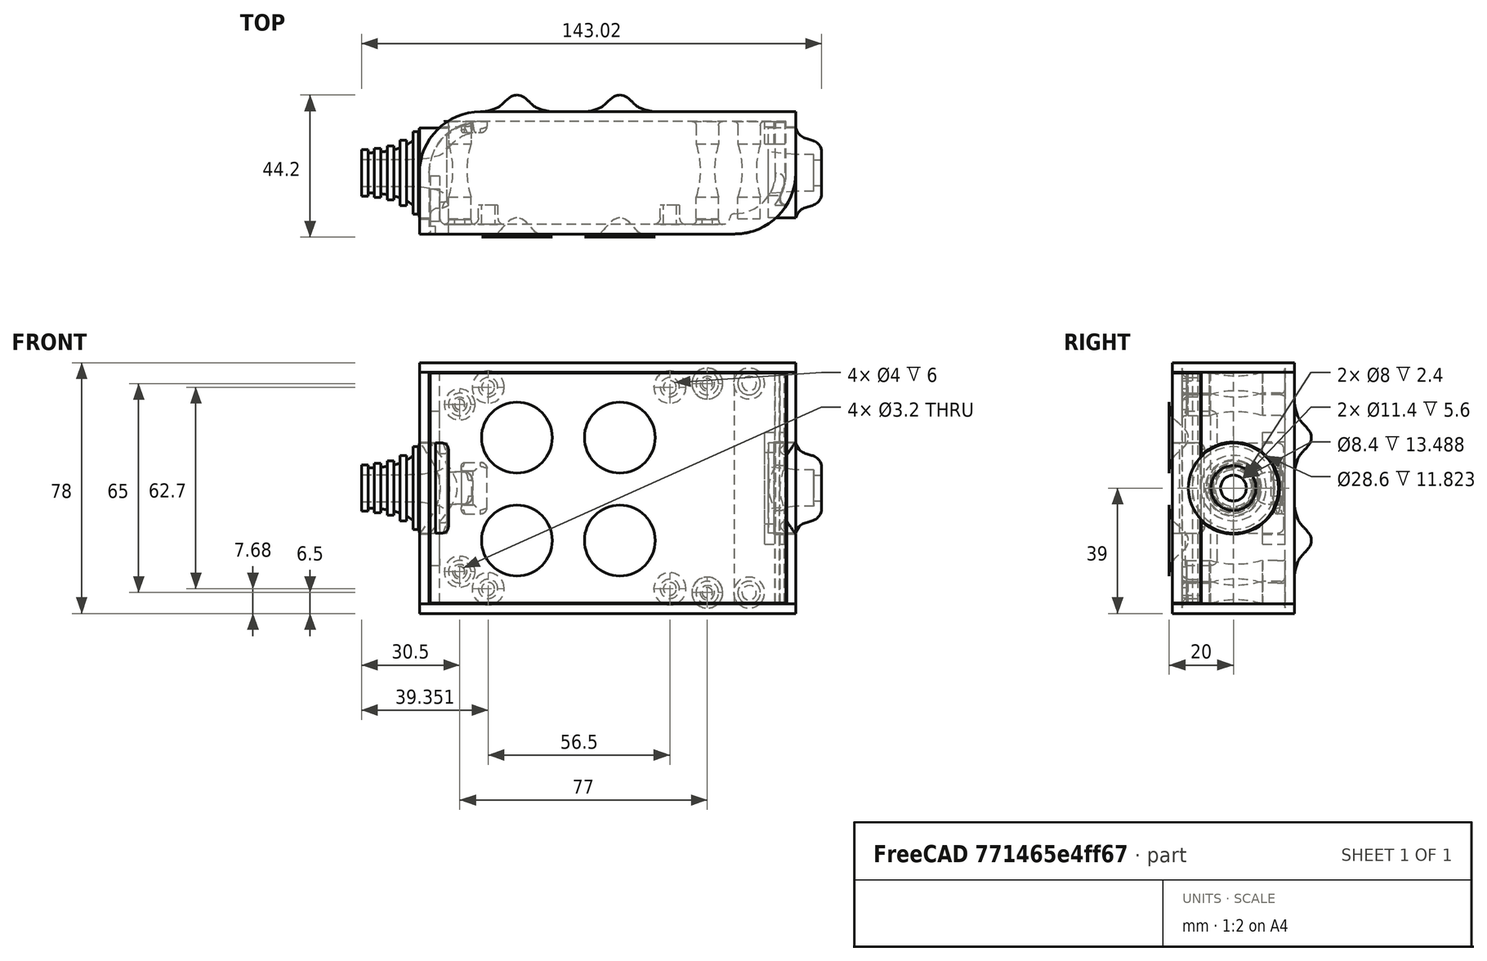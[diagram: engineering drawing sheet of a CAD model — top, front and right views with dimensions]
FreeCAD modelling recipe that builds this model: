
FCSTD DOCUMENT  (FreeCAD 0.19R0.19.2)
Label: enclosure_068
License: All rights reserved
LicenseURL: http://en.wikipedia.org/wiki/All_rights_reserved
objects: Part::Feature×47, Part::MultiFuse×44, Part::Revolution×44, Part::Fillet×22, Part::Cylinder×22, Sketcher::SketchObject×17, Part::Cut×14, Part::Extrusion×10, Part::Box×10, App::MeasureDistance×2
note: 230 computed .brp shape members not serialized (recipe doc carries the construction recipe); baked Part::Feature solids carry a one-line shape summary decoded from their .brp

FEATURE [Sketcher::SketchObject] Sketch  label="topSketch"
  FullyConstrained = true
  sketch-geometry (13):
    g0: LineSegment StartX=117 StartY=19 StartZ=0 EndX=117 EndY=38 EndZ=0
    g1: ArcOfCircle CenterX=98 CenterY=19 CenterZ=0 NormalX=0 NormalY=0 NormalZ=1 AngleXU=0 Radius=19 StartAngle=5.7297 EndAngle=6.28319
    g2: LineSegment StartX=0 StartY=3 StartZ=0 EndX=0 EndY=19 EndZ=0
    g3: LineSegment StartX=19 StartY=38 StartZ=0 EndX=117 EndY=38 EndZ=0
    g4: ArcOfCircle CenterX=19 CenterY=19 CenterZ=0 NormalX=0 NormalY=0 NormalZ=1 AngleXU=0 Radius=19 StartAngle=1.5708 EndAngle=3.14159
    g5: ArcOfCircle CenterX=19 CenterY=19 CenterZ=0 NormalX=0 NormalY=0 NormalZ=1 AngleXU=0 Radius=16 StartAngle=1.5708 EndAngle=3.14159
    g6: ArcOfCircle CenterX=98 CenterY=19 CenterZ=0 NormalX=0 NormalY=0 NormalZ=1 AngleXU=0 Radius=16 StartAngle=5.60905 EndAngle=6.28319
    g7: LineSegment StartX=114 StartY=19 StartZ=0 EndX=114 EndY=35 EndZ=0
    g8: LineSegment StartX=110.5 StartY=9.01251 StartZ=0 EndX=114.163 EndY=9.01251 EndZ=0
    g9: LineSegment StartX=114 StartY=35 StartZ=0 EndX=19 EndY=35 EndZ=0
    g10: LineSegment StartX=0 StartY=3 StartZ=0 EndX=0 EndY=0 EndZ=0
    g11: LineSegment StartX=3 StartY=0 StartZ=0 EndX=0 EndY=0 EndZ=0
    g12: LineSegment StartX=3 StartY=19 StartZ=0 EndX=3 EndY=0 EndZ=0
  constraints (33):
    c: Vertical(g0)
    c: Distance(g0) = 19
    c: Block(g0)
    c: Coincident(g1,g0)
    c: Block(g1)
    c: Vertical(g2)
    c: Block(g2)
    c: Coincident(g3,g0)
    c: Horizontal(g3)
    c: Distance(g3) = 98
    c: Coincident(g4,g3)
    c: Coincident(g4,g2)
    c: Block(g4)
    c: Coincident(g5,g4)
    c: Coincident(g6,g1)
    c: Block(g6)
    c: Block(g5)
    c: Coincident(g7,g6)
    c: Vertical(g7)
    c: Coincident(g8,g6)
    c: Coincident(g8,g1)
    c: Coincident(g9,g7)
    c: Coincident(g9,g5)
    c: Horizontal(g9)
    c: Tangent(g9,g5)
    c: Coincident(g10,g2)
    c: Distance(g10) = 3
    c: Vertical(g10)
    c: Coincident(g11,g10)
    c: Horizontal(g11)
    c: Coincident(g12,g5)
    c: Coincident(g12,g11)
    c: Vertical(g12)
FEATURE [Sketcher::SketchObject] Sketch001  label="bottomSketch"
  FullyConstrained = true
  sketch-geometry (32):
    g0: LineSegment StartX=3.3 StartY=-6.03275e-07 StartZ=0 EndX=98 EndY=-6.03275e-07 EndZ=0
    g1: ArcOfCircle CenterX=98 CenterY=19 CenterZ=0 NormalX=0 NormalY=0 NormalZ=1 AngleXU=0 Radius=19 StartAngle=4.71239 EndAngle=5.71103
    g2: LineSegment StartX=6.3 StartY=8 StartZ=0 EndX=3.3 EndY=8 EndZ=0
    g3: LineSegment StartX=3.3 StartY=8 StartZ=0 EndX=3.3 EndY=-6.03275e-07 EndZ=0
    g4: ArcOfCircle CenterX=8.3 CenterY=5 CenterZ=0 NormalX=0 NormalY=0 NormalZ=1 AngleXU=0 Radius=2 StartAngle=3.14159 EndAngle=4.71239
    g5: LineSegment StartX=6.3 StartY=8 StartZ=0 EndX=6.3 EndY=5 EndZ=0
    g6: ArcOfCircle CenterX=98 CenterY=19 CenterZ=0 NormalX=0 NormalY=0 NormalZ=1 AngleXU=0 Radius=12.7 StartAngle=4.71239 EndAngle=6.28319
    g7: LineSegment StartX=94.7 StartY=3 StartZ=0 EndX=8.3 EndY=3 EndZ=0
    g8-g12: Circle x5 (B-spline internal-alignment scaffolding for g13; pole/knot coordinates omitted)
    g13: BSplineCurve PolesCount=5 KnotsCount=3 Degree=3 IsPeriodic=0
    g14: GeomPoint X=98 Y=6.3 Z=0
    g15: GeomPoint X=96.3938 Y=4.71946 Z=0
    g16: GeomPoint X=94.7 Y=3 Z=0
    g17-g23: Circle x7 (B-spline internal-alignment scaffolding for g24; pole/knot coordinates omitted)
    g24: BSplineCurve PolesCount=7 KnotsCount=5 Degree=3 IsPeriodic=0
    g25-g29: GeomPoint x5 (B-spline internal-alignment scaffolding for g24; pole/knot coordinates omitted)
    g30: ArcOfCircle CenterX=98 CenterY=19 CenterZ=0 NormalX=0 NormalY=0 NormalZ=1 AngleXU=0 Radius=15.7 StartAngle=5.81226 EndAngle=6.28319
    g31: LineSegment StartX=110.7 StartY=19 StartZ=0 EndX=113.7 EndY=19 EndZ=0
  constraints (41):
    c: Horizontal(g0)
    c: Coincident(g1,g0)
    c: Block(g1)
    c: Horizontal(g2)
    c: Distance(g2) = 3
    c: Coincident(g3,g2)
    c: Vertical(g3)
    c: Coincident(g3,g0)
    c: Block(g4)
    c: Block(g2)
    c: Coincident(g5,g2)
    c: Coincident(g5,g4)
    c: Vertical(g5)
    c: Coincident(g6,g1)
    c: Block(g6)
    c: Coincident(g7,g4)
    c: Horizontal(g7)
    c: Block(g0)
    c: Block(g7)
    c: Block(g3)
    c: Coincident(g13,g6)
    c: Weight(g8) = 1
    c: Equal(g8, g9-g12) x4
    c: Coincident(g13,g7)
    c: InternalAlignment(g8-g12 -> g13) x5
    c: InternalAlignment(g14,g13)
    c: InternalAlignment(g15,g13)
    c: InternalAlignment(g16,g13)
    c: Block(g13)
    c: Weight(g17) = 1
    c: Equal(g17, g18-g23) x6
    c: Coincident(g24,g1)
    c: InternalAlignment(g17-g23 -> g24) x7
    c: InternalAlignment(g25-g29 -> g24) x5
    c: Block(g24)
    c: Coincident(g30,g24)
    c: Coincident(g31,g6)
    c: Coincident(g31,g30)
    c: Horizontal(g31)
    c: Block(g31)
    c: Block(g30)
FEATURE [Part::Extrusion] Extrude  label="top"
  Base = -> Sketch
  Dir = (0,0,1)
  DirMode = 2
  FaceMakerClass = Part::FaceMakerBullseye
  LengthFwd = 72
  LengthRev = 0
  Solid = true
  Symmetric = false
FEATURE [Part::Extrusion] Extrude001  label="bottom"
  Base = -> Sketch001
  Dir = (0,0,1)
  DirMode = 2
  FaceMakerClass = Part::FaceMakerBullseye
  LengthFwd = 71.4
  LengthRev = 0
  Placement = pos=(0,0,0.3) rot=(0,0,1;0rad)
  Solid = true
  Symmetric = false
FEATURE [Sketcher::SketchObject] Sketch002  label="topSketch001"
  FullyConstrained = true
  sketch-geometry (6):
    g0: LineSegment StartX=19 StartY=38 StartZ=0 EndX=117 EndY=38 EndZ=0
    g1: ArcOfCircle CenterX=19 CenterY=19 CenterZ=0 NormalX=0 NormalY=0 NormalZ=1 AngleXU=0 Radius=19 StartAngle=1.5708 EndAngle=3.14159
    g2: LineSegment StartX=117 StartY=38 StartZ=0 EndX=117 EndY=19 EndZ=0
    g3: LineSegment StartX=98 StartY=1.0161e-12 StartZ=0 EndX=5.22862e-06 EndY=1.0161e-12 EndZ=0
    g4: LineSegment StartX=5.22862e-06 StartY=19 StartZ=0 EndX=5.22862e-06 EndY=1.0161e-12 EndZ=0
    g5: ArcOfCircle CenterX=98 CenterY=19 CenterZ=0 NormalX=0 NormalY=0 NormalZ=1 AngleXU=0 Radius=19 StartAngle=4.71239 EndAngle=6.28319
  constraints (16):
    c: Horizontal(g0)
    c: Distance(g0) = 98
    c: Coincident(g1,g0)
    c: Block(g1)
    c: Coincident(g2,g0)
    c: Vertical(g2)
    c: Distance(g2) = 19
    c: Horizontal(g3)
    c: Coincident(g4,g1)
    c: Vertical(g4)
    c: Coincident(g3,g4)
    c: Block(g3)
    c: Coincident(g5,g2)
    c: Coincident(g5,g3)
    c: Block(g0)
    c: Block(g5)
FEATURE [Part::Extrusion] Extrude002  label="sideA"
  Base = -> Sketch002
  Dir = (0,0,1)
  DirMode = 2
  FaceMakerClass = Part::FaceMakerBullseye
  LengthFwd = 3
  LengthRev = 0
  Placement = pos=(0,0,-3) rot=(0,0,1;0rad)
  Solid = true
  Symmetric = false
FEATURE [Sketcher::SketchObject] Sketch003  label="topSketch002"
  FullyConstrained = true
  sketch-geometry (6):
    g0: LineSegment StartX=19 StartY=38 StartZ=0 EndX=117 EndY=38 EndZ=0
    g1: ArcOfCircle CenterX=19 CenterY=19 CenterZ=0 NormalX=0 NormalY=0 NormalZ=1 AngleXU=0 Radius=19 StartAngle=1.5708 EndAngle=3.14159
    g2: LineSegment StartX=117 StartY=38 StartZ=0 EndX=117 EndY=19 EndZ=0
    g3: LineSegment StartX=98 StartY=1.0161e-12 StartZ=0 EndX=5.22862e-06 EndY=1.0161e-12 EndZ=0
    g4: LineSegment StartX=5.22862e-06 StartY=19 StartZ=0 EndX=5.22862e-06 EndY=1.0161e-12 EndZ=0
    g5: ArcOfCircle CenterX=98 CenterY=19 CenterZ=0 NormalX=0 NormalY=0 NormalZ=1 AngleXU=0 Radius=19 StartAngle=4.71239 EndAngle=6.28319
  constraints (16):
    c: Horizontal(g0)
    c: Distance(g0) = 98
    c: Coincident(g1,g0)
    c: Block(g1)
    c: Coincident(g2,g0)
    c: Vertical(g2)
    c: Distance(g2) = 19
    c: Horizontal(g3)
    c: Coincident(g4,g1)
    c: Vertical(g4)
    c: Coincident(g3,g4)
    c: Block(g3)
    c: Coincident(g5,g2)
    c: Coincident(g5,g3)
    c: Block(g0)
    c: Block(g5)
FEATURE [Part::Extrusion] Extrude003  label="sideB"
  Base = -> Sketch003
  Dir = (0,0,1)
  DirMode = 2
  FaceMakerClass = Part::FaceMakerBullseye
  LengthFwd = 3
  LengthRev = 0
  Placement = pos=(0,0,72) rot=(0,0,1;0rad)
  Solid = true
  Symmetric = false
FEATURE [Sketcher::SketchObject] Sketch004
  FullyConstrained = true
  MapMode = 3
  Placement = pos=(0,0,0) rot=(1,0,0;1.5708rad)
  Support = -> [Extrude]
  sketch-geometry (8):
    g0: Circle CenterX=80.351 CenterY=-67.6202 CenterZ=0 NormalX=0 NormalY=0 NormalZ=1 AngleXU=0 Radius=2
    g1: Circle CenterX=80.351 CenterY=-67.6202 CenterZ=0 NormalX=0 NormalY=0 NormalZ=1 AngleXU=0 Radius=3
    g2: Circle CenterX=80.351 CenterY=-4.92017 CenterZ=0 NormalX=0 NormalY=0 NormalZ=1 AngleXU=0 Radius=2
    g3: Circle CenterX=80.351 CenterY=-4.92017 CenterZ=0 NormalX=0 NormalY=0 NormalZ=1 AngleXU=0 Radius=3
    g4: Circle CenterX=23.851 CenterY=-4.92017 CenterZ=0 NormalX=0 NormalY=0 NormalZ=1 AngleXU=0 Radius=2
    g5: Circle CenterX=23.851 CenterY=-4.92017 CenterZ=0 NormalX=0 NormalY=0 NormalZ=1 AngleXU=0 Radius=3
    g6: Circle CenterX=23.851 CenterY=-67.6202 CenterZ=0 NormalX=0 NormalY=0 NormalZ=1 AngleXU=0 Radius=2
    g7: Circle CenterX=23.851 CenterY=-67.6202 CenterZ=0 NormalX=0 NormalY=0 NormalZ=1 AngleXU=0 Radius=3
  constraints (8):
    c: Block(g3)
    c: Block(g2)
    c: Block(g1)
    c: Block(g0)
    c: Block(g6)
    c: Block(g7)
    c: Block(g4)
    c: Block(g5)
FEATURE [Part::Extrusion] Extrude004
  Base = -> Sketch004
  Dir = (0,-1,2e-16)
  DirMode = 2
  FaceMakerClass = Part::FaceMakerBullseye
  LengthFwd = 6
  LengthRev = 0
  Placement = pos=(0,9,0) rot=(0,0,1;0rad)
  Solid = true
  Symmetric = false
FEATURE [Sketcher::SketchObject] Sketch005
  FullyConstrained = true
  MapMode = 3
  Placement = pos=(0,0,0) rot=(1,0,0;1.5708rad)
  Support = -> [Extrude]
  sketch-geometry (8):
    g0: Circle CenterX=80.351 CenterY=-67.6202 CenterZ=0 NormalX=0 NormalY=0 NormalZ=1 AngleXU=0 Radius=3
    g1: Circle CenterX=80.351 CenterY=-4.92017 CenterZ=0 NormalX=0 NormalY=0 NormalZ=1 AngleXU=0 Radius=3
    g2: Circle CenterX=23.851 CenterY=-4.92017 CenterZ=0 NormalX=0 NormalY=0 NormalZ=1 AngleXU=0 Radius=3
    g3: Circle CenterX=23.851 CenterY=-67.6202 CenterZ=0 NormalX=0 NormalY=0 NormalZ=1 AngleXU=0 Radius=3
    g4: Circle CenterX=23.851 CenterY=-67.6202 CenterZ=0 NormalX=0 NormalY=0 NormalZ=1 AngleXU=0 Radius=5
    g5: Circle CenterX=80.351 CenterY=-67.6202 CenterZ=0 NormalX=0 NormalY=0 NormalZ=1 AngleXU=0 Radius=5
    g6: Circle CenterX=23.851 CenterY=-4.92017 CenterZ=0 NormalX=0 NormalY=0 NormalZ=1 AngleXU=0 Radius=5
    g7: Circle CenterX=80.351 CenterY=-4.92017 CenterZ=0 NormalX=0 NormalY=0 NormalZ=1 AngleXU=0 Radius=5
  constraints (8):
    c: Block(g1)
    c: Block(g0)
    c: Block(g3)
    c: Block(g2)
    c: Block(g5)
    c: Block(g4)
    c: Block(g6)
    c: Block(g7)
FEATURE [Part::Extrusion] Extrude005
  Base = -> Sketch005
  Dir = (0,-1,2e-16)
  DirMode = 2
  FaceMakerClass = Part::FaceMakerBullseye
  LengthFwd = 2
  LengthRev = 0
  Solid = true
  Symmetric = false
FEATURE [Sketcher::SketchObject] Sketch006
  FullyConstrained = true
  MapMode = 3
  Placement = pos=(0,0,0) rot=(1,0,0;1.5708rad)
  sketch-geometry (8):
    g0: Circle CenterX=80.351 CenterY=-67.6202 CenterZ=0 NormalX=0 NormalY=0 NormalZ=1 AngleXU=0 Radius=3
    g1: Circle CenterX=80.351 CenterY=-4.92017 CenterZ=0 NormalX=0 NormalY=0 NormalZ=1 AngleXU=0 Radius=3
    g2: Circle CenterX=23.851 CenterY=-4.92017 CenterZ=0 NormalX=0 NormalY=0 NormalZ=1 AngleXU=0 Radius=3
    g3: Circle CenterX=23.851 CenterY=-67.6202 CenterZ=0 NormalX=0 NormalY=0 NormalZ=1 AngleXU=0 Radius=3
    g4: Circle CenterX=23.851 CenterY=-67.6202 CenterZ=0 NormalX=0 NormalY=0 NormalZ=1 AngleXU=0 Radius=5
    g5: Circle CenterX=80.351 CenterY=-67.6202 CenterZ=0 NormalX=0 NormalY=0 NormalZ=1 AngleXU=0 Radius=5
    g6: Circle CenterX=23.851 CenterY=-4.92017 CenterZ=0 NormalX=0 NormalY=0 NormalZ=1 AngleXU=0 Radius=5
    g7: Circle CenterX=80.351 CenterY=-4.92017 CenterZ=0 NormalX=0 NormalY=0 NormalZ=1 AngleXU=0 Radius=5
  constraints (8):
    c: Block(g1)
    c: Block(g0)
    c: Block(g3)
    c: Block(g2)
    c: Block(g5)
    c: Block(g4)
    c: Block(g6)
    c: Block(g7)
FEATURE [Part::Extrusion] Extrude007
  Base = -> Sketch006
  Dir = (0,-1,2e-16)
  DirMode = 2
  FaceMakerClass = Part::FaceMakerBullseye
  LengthFwd = 2
  LengthRev = 0
  Solid = true
  Symmetric = false
FEATURE [Part::Fillet] Fillet
  Base = -> Extrude007
  Edges = 4 edges r=1.99: [Edge6,Edge12,Edge18,Edge24]
FEATURE [Part::Cut] Cut
  Base = -> Extrude005
  Placement = pos=(0,5,0) rot=(0,0,1;0rad)
  Tool = -> Fillet
FEATURE [Part::MultiFuse] Fusion  label="pCBScrews"
  Placement = pos=(-2.5,0,72.3) rot=(0,0,1;0rad)
  Shapes = -> [Extrude004,Cut]
FEATURE [App::MeasureDistance] Distance  label="Distance: 0.69 mm"
  Distance = 0.685967
  P1 = (24.0138,2.9647,0.3)
  P2 = (23.8901,3,-0.373787)
FEATURE [App::MeasureDistance] Distance001  label="Distance: 0.53 mm"
  Distance = 0.533607
  P1 = (80.2939,3,72.2334)
  P2 = (80.281,2.99661,71.7)
FEATURE [Part::Fillet] Fillet001
  Base = -> Extrude001
  Edges = 1 edges r=2.4: [Edge17]
FEATURE [Part::Fillet] Fillet002  label="bottom001"
  Base = -> Fillet001
  Edges = 1 edges r=2.4: [Edge36]
FEATURE [Part::Fillet] Fillet003  label="top001"
  Base = -> Extrude
  Edges = 1 edges r=2: [Edge1]
FEATURE [Sketcher::SketchObject] Sketch007
  FullyConstrained = true
  sketch-geometry (16):
    g0: LineSegment StartX=4 StartY=0 StartZ=0 EndX=4 EndY=2.4 EndZ=0
    g1: LineSegment StartX=4 StartY=2.4 StartZ=0 EndX=7 EndY=2.4 EndZ=0
    g2: LineSegment StartX=4 StartY=0 StartZ=0 EndX=5.7 EndY=0 EndZ=0
    g3: LineSegment StartX=5.7 StartY=0 StartZ=0 EndX=5.7 EndY=-5.6 EndZ=0
    g4-g8: Circle x5 (B-spline internal-alignment scaffolding for g9; pole/knot coordinates omitted)
    g9: BSplineCurve PolesCount=5 KnotsCount=3 Degree=3 IsPeriodic=0
    g10: GeomPoint X=7 Y=2.4 Z=0
    g11: GeomPoint X=10.4582 Y=-1.55472 Z=0
    g12: GeomPoint X=14 Y=-5.6 Z=0
    g13: LineSegment StartX=14 StartY=-5.6 StartZ=0 EndX=14 EndY=-14.1 EndZ=0
    g14: LineSegment StartX=14 StartY=-14.1 StartZ=0 EndX=6.5 EndY=-14.1 EndZ=0
    g15: LineSegment StartX=5.7 StartY=-5.6 StartZ=0 EndX=6.5 EndY=-14.1 EndZ=0
  constraints (28):
    c: Distance(g0) = 2.4
    c: Vertical(g0)
    c: Block(g0)
    c: Coincident(g1,g0)
    c: Horizontal(g1)
    c: Distance(g1) = 3
    c: Coincident(g2,g0)
    c: Horizontal(g2)
    c: Distance(g2) = 1.7
    c: Coincident(g3,g2)
    c: Vertical(g3)
    c: Distance(g3) = 5.6
    c: Coincident(g9,g1)
    c: Weight(g4) = 1
    c: Equal(g4, g5-g8) x4
    c: InternalAlignment(g4-g8 -> g9) x5
    c: InternalAlignment(g10,g9)
    c: InternalAlignment(g11,g9)
    c: InternalAlignment(g12,g9)
    c: Block(g9)
    c: Coincident(g13,g9)
    c: Vertical(g13)
    c: Distance(g13) = 8.5
    c: Coincident(g14,g13)
    c: Horizontal(g14)
    c: Distance(g14) = 7.5
    c: Coincident(g15,g3)
    c: Coincident(g15,g14)
FEATURE [Part::Feature] Face
  shape: bbox 10 x 16.5 x 2e-07 mm, 1 faces, 0 solids (baked)
FEATURE [Part::Revolution] Revolve  label="plugHousing"
  Angle = 360
  Axis = (0,1,0)
  Base = (0,0,0)
  FaceMakerClass = Part::FaceMakerBullseye
  Placement = pos=(0,0,36.15) rot=(0,0,1;0rad)
  Solid = false
  Source = -> Face
  Symmetric = false
FEATURE [Part::Feature] Face001
  shape: bbox 10 x 16.5 x 2e-07 mm, 1 faces, 0 solids (baked)
FEATURE [Part::Revolution] Revolve001  label="plugHousing001"
  Angle = 360
  Axis = (0,1,0)
  Base = (0,0,0)
  FaceMakerClass = Part::FaceMakerBullseye
  Placement = pos=(0,0,36.15) rot=(0,0,1;0rad)
  Solid = false
  Source = -> Face001
  Symmetric = false
FEATURE [Part::MultiFuse] Fusion001  label="plugHousing002"
  Placement = pos=(0,0,0) rot=(0,0,1;1.5708rad)
  Shapes = -> [Revolve001,Revolve]
FEATURE [Part::Feature] Face002
  shape: bbox 10 x 16.5 x 2e-07 mm, 1 faces, 0 solids (baked)
FEATURE [Part::Revolution] Revolve003  label="plugHousing005"
  Angle = 360
  Axis = (0,1,0)
  Base = (0,0,0)
  FaceMakerClass = Part::FaceMakerBullseye
  Placement = pos=(0,0,36.15) rot=(0,0,1;0rad)
  Solid = false
  Source = -> Face002
  Symmetric = false
FEATURE [Part::Feature] Face003
  shape: bbox 10 x 16.5 x 2e-07 mm, 1 faces, 0 solids (baked)
FEATURE [Part::Revolution] Revolve002  label="plugHousing003"
  Angle = 360
  Axis = (0,1,0)
  Base = (0,0,0)
  FaceMakerClass = Part::FaceMakerBullseye
  Placement = pos=(0,0,36.15) rot=(0,0,1;0rad)
  Solid = false
  Source = -> Face003
  Symmetric = false
FEATURE [Part::MultiFuse] Fusion002  label="plugHousing004"
  Placement = pos=(0,0,0) rot=(0,0,1;1.5708rad)
  Shapes = -> [Revolve002,Revolve003]
FEATURE [Part::MultiFuse] Fusion003  label="plugHousing006"
  Placement = pos=(0,19,0) rot=(0,0,1;3.14159rad)
  Shapes = -> [Fusion002,Fusion001]
FEATURE [Part::Feature] Face004
  shape: bbox 10 x 16.5 x 2e-07 mm, 1 faces, 0 solids (baked)
FEATURE [Part::Revolution] Revolve006  label="plugHousing010"
  Angle = 360
  Axis = (0,1,0)
  Base = (0,0,0)
  FaceMakerClass = Part::FaceMakerBullseye
  Placement = pos=(0,0,36.15) rot=(0,0,1;0rad)
  Solid = false
  Source = -> Face004
  Symmetric = false
FEATURE [Part::Feature] Face005
  shape: bbox 10 x 16.5 x 2e-07 mm, 1 faces, 0 solids (baked)
FEATURE [Part::Revolution] Revolve007  label="plugHousing011"
  Angle = 360
  Axis = (0,1,0)
  Base = (0,0,0)
  FaceMakerClass = Part::FaceMakerBullseye
  Placement = pos=(0,0,36.15) rot=(0,0,1;0rad)
  Solid = false
  Source = -> Face005
  Symmetric = false
FEATURE [Part::Feature] Face006
  shape: bbox 10 x 16.5 x 2e-07 mm, 1 faces, 0 solids (baked)
FEATURE [Part::Revolution] Revolve004  label="plugHousing007"
  Angle = 360
  Axis = (0,1,0)
  Base = (0,0,0)
  FaceMakerClass = Part::FaceMakerBullseye
  Placement = pos=(0,0,36.15) rot=(0,0,1;0rad)
  Solid = false
  Source = -> Face006
  Symmetric = false
FEATURE [Part::MultiFuse] Fusion004  label="plugHousing009"
  Placement = pos=(0,0,0) rot=(0,0,1;1.5708rad)
  Shapes = -> [Revolve004,Revolve007]
FEATURE [Part::Feature] Face007
  shape: bbox 10 x 16.5 x 2e-07 mm, 1 faces, 0 solids (baked)
FEATURE [Part::Revolution] Revolve005  label="plugHousing008"
  Angle = 360
  Axis = (0,1,0)
  Base = (0,0,0)
  FaceMakerClass = Part::FaceMakerBullseye
  Placement = pos=(0,0,36.15) rot=(0,0,1;0rad)
  Solid = false
  Source = -> Face007
  Symmetric = false
FEATURE [Part::MultiFuse] Fusion005  label="plugHousing012"
  Placement = pos=(0,0,0) rot=(0,0,1;1.5708rad)
  Shapes = -> [Revolve006,Revolve005]
FEATURE [Part::MultiFuse] Fusion006  label="plugHousing013"
  Placement = pos=(0,19,0) rot=(0,0,1;3.14159rad)
  Shapes = -> [Fusion005,Fusion004]
FEATURE [Part::MultiFuse] Fusion007  label="plugHousing014"
  Placement = pos=(122.621,0,-0.15) rot=(0,0,1;0rad)
  Shapes = -> [Fusion003,Fusion006]
FEATURE [Part::Cylinder] Cylinder002
  Angle = 360
  AttacherType = Attacher::AttachEngine3D
  Height = 20
  Placement = pos=(0,0,36.15) rot=(0,0,1;0rad)
  Radius = 4
FEATURE [Part::Cylinder] Cylinder003
  Angle = 360
  AttacherType = Attacher::AttachEngine3D
  Height = 10
  Placement = pos=(0,0,36.15) rot=(0,0,1;0rad)
  Radius = 4
FEATURE [Part::MultiFuse] Fusion009  label="removeToCreateHoleForPlugHousing"
  Placement = pos=(70,19,36.15) rot=(0,1,0;1.5708rad)
  Shapes = -> [Cylinder002,Cylinder003]
FEATURE [Part::Cylinder] Cylinder004
  Angle = 360
  AttacherType = Attacher::AttachEngine3D
  Height = 20
  Placement = pos=(0,0,36.15) rot=(0,0,1;0rad)
  Radius = 4
FEATURE [Part::Cylinder] Cylinder005
  Angle = 360
  AttacherType = Attacher::AttachEngine3D
  Height = 10
  Placement = pos=(0,0,36.15) rot=(0,0,1;0rad)
  Radius = 4
FEATURE [Part::MultiFuse] Fusion010  label="removeToCreateHoleForPlugHousing001"
  Placement = pos=(70,19,36.15) rot=(0,1,0;1.5708rad)
  Shapes = -> [Cylinder004,Cylinder005]
FEATURE [Part::Cut] Cut001
  Base = -> Fillet003
  Tool = -> Fusion010
FEATURE [Part::Cut] Cut002  label="Bottom"
  Base = -> Fillet002
  Tool = -> Fusion009
FEATURE [Part::Feature] Face008
  shape: bbox 10 x 16.5 x 2e-07 mm, 1 faces, 0 solids (baked)
FEATURE [Part::Revolution] Revolve011  label="plugHousing021"
  Angle = 360
  Axis = (0,1,0)
  Base = (0,0,0)
  FaceMakerClass = Part::FaceMakerBullseye
  Placement = pos=(0,0,36.15) rot=(0,0,1;0rad)
  Solid = false
  Source = -> Face008
  Symmetric = false
FEATURE [Part::Feature] Face009
  shape: bbox 10 x 16.5 x 2e-07 mm, 1 faces, 0 solids (baked)
FEATURE [Part::Revolution] Revolve012  label="plugHousing022"
  Angle = 360
  Axis = (0,1,0)
  Base = (0,0,0)
  FaceMakerClass = Part::FaceMakerBullseye
  Placement = pos=(0,0,36.15) rot=(0,0,1;0rad)
  Solid = false
  Source = -> Face009
  Symmetric = false
FEATURE [Part::Feature] Face010
  shape: bbox 10 x 16.5 x 2e-07 mm, 1 faces, 0 solids (baked)
FEATURE [Part::Feature] Face011
  shape: bbox 10 x 16.5 x 2e-07 mm, 1 faces, 0 solids (baked)
FEATURE [Part::Revolution] Revolve014  label="plugHousing026"
  Angle = 360
  Axis = (0,1,0)
  Base = (0,0,0)
  FaceMakerClass = Part::FaceMakerBullseye
  Placement = pos=(0,0,36.15) rot=(0,0,1;0rad)
  Solid = false
  Source = -> Face011
  Symmetric = false
FEATURE [Part::Feature] Face012
  shape: bbox 10 x 16.5 x 2e-07 mm, 1 faces, 0 solids (baked)
FEATURE [Part::Revolution] Revolve009  label="plugHousing016"
  Angle = 360
  Axis = (0,1,0)
  Base = (0,0,0)
  FaceMakerClass = Part::FaceMakerBullseye
  Placement = pos=(0,0,36.15) rot=(0,0,1;0rad)
  Solid = false
  Source = -> Face012
  Symmetric = false
FEATURE [Part::Feature] Face013
  shape: bbox 10 x 16.5 x 2e-07 mm, 1 faces, 0 solids (baked)
FEATURE [Part::Revolution] Revolve015  label="plugHousing027"
  Angle = 360
  Axis = (0,1,0)
  Base = (0,0,0)
  FaceMakerClass = Part::FaceMakerBullseye
  Placement = pos=(0,0,36.15) rot=(0,0,1;0rad)
  Solid = false
  Source = -> Face013
  Symmetric = false
FEATURE [Part::Feature] Face014
  shape: bbox 10 x 16.5 x 2e-07 mm, 1 faces, 0 solids (baked)
FEATURE [Part::Revolution] Revolve010  label="plugHousing017"
  Angle = 360
  Axis = (0,1,0)
  Base = (0,0,0)
  FaceMakerClass = Part::FaceMakerBullseye
  Placement = pos=(0,0,36.15) rot=(0,0,1;0rad)
  Solid = false
  Source = -> Face014
  Symmetric = false
FEATURE [Part::MultiFuse] Fusion015  label="plugHousing024"
  Placement = pos=(0,0,0) rot=(0,0,1;1.5708rad)
  Shapes = -> [Revolve010,Revolve015]
FEATURE [Part::Feature] Face015
  shape: bbox 10 x 16.5 x 2e-07 mm, 1 faces, 0 solids (baked)
FEATURE [Part::Revolution] Revolve013  label="plugHousing025"
  Angle = 360
  Axis = (0,1,0)
  Base = (0,0,0)
  FaceMakerClass = Part::FaceMakerBullseye
  Placement = pos=(0,0,36.15) rot=(0,0,1;0rad)
  Solid = false
  Source = -> Face015
  Symmetric = false
FEATURE [Part::MultiFuse] Fusion011  label="plugHousing018"
  Placement = pos=(0,0,0) rot=(0,0,1;1.5708rad)
  Shapes = -> [Revolve014,Revolve013]
FEATURE [Part::MultiFuse] Fusion012  label="plugHousing019"
  Placement = pos=(0,19,0) rot=(0,0,1;3.14159rad)
  Shapes = -> [Fusion011,Fusion015]
FEATURE [Part::Feature] Face016
  shape: bbox 10 x 16.5 x 2e-07 mm, 1 faces, 0 solids (baked)
FEATURE [Part::Revolution] Revolve019  label="plugHousing033"
  Angle = 360
  Axis = (0,1,0)
  Base = (0,0,0)
  FaceMakerClass = Part::FaceMakerBullseye
  Placement = pos=(0,0,36.15) rot=(0,0,1;0rad)
  Solid = false
  Source = -> Face016
  Symmetric = false
FEATURE [Part::Feature] Face017
  shape: bbox 10 x 16.5 x 2e-07 mm, 1 faces, 0 solids (baked)
FEATURE [Part::Revolution] Revolve020  label="plugHousing034"
  Angle = 360
  Axis = (0,1,0)
  Base = (0,0,0)
  FaceMakerClass = Part::FaceMakerBullseye
  Placement = pos=(0,0,36.15) rot=(0,0,1;0rad)
  Solid = false
  Source = -> Face017
  Symmetric = false
FEATURE [Part::Feature] Face018
  shape: bbox 10 x 16.5 x 2e-07 mm, 1 faces, 0 solids (baked)
FEATURE [Part::Revolution] Revolve016  label="plugHousing030"
  Angle = 360
  Axis = (0,1,0)
  Base = (0,0,0)
  FaceMakerClass = Part::FaceMakerBullseye
  Placement = pos=(0,0,36.15) rot=(0,0,1;0rad)
  Solid = false
  Source = -> Face018
  Symmetric = false
FEATURE [Part::MultiFuse] Fusion020  label="plugHousing038"
  Placement = pos=(0,0,0) rot=(0,0,1;1.5708rad)
  Shapes = -> [Revolve016,Revolve020]
FEATURE [Part::Feature] Face019
  shape: bbox 10 x 16.5 x 2e-07 mm, 1 faces, 0 solids (baked)
FEATURE [Part::Feature] Face020
  shape: bbox 10 x 16.5 x 2e-07 mm, 1 faces, 0 solids (baked)
FEATURE [Part::Revolution] Revolve017  label="plugHousing031"
  Angle = 360
  Axis = (0,1,0)
  Base = (0,0,0)
  FaceMakerClass = Part::FaceMakerBullseye
  Placement = pos=(0,0,36.15) rot=(0,0,1;0rad)
  Solid = false
  Source = -> Face020
  Symmetric = false
FEATURE [Part::MultiFuse] Fusion021  label="plugHousing039"
  Placement = pos=(0,0,0) rot=(0,0,1;1.5708rad)
  Shapes = -> [Revolve019,Revolve017]
FEATURE [Part::MultiFuse] Fusion023  label="plugHousing041"
  Placement = pos=(0,19,0) rot=(0,0,1;3.14159rad)
  Shapes = -> [Fusion021,Fusion020]
FEATURE [Part::Revolution] Revolve022  label="plugHousing043"
  Angle = 360
  Axis = (0,1,0)
  Base = (0,0,0)
  FaceMakerClass = Part::FaceMakerBullseye
  Placement = pos=(0,0,36.15) rot=(0,0,1;0rad)
  Solid = false
  Source = -> Face019
  Symmetric = false
FEATURE [Part::Feature] Face021
  shape: bbox 10 x 16.5 x 2e-07 mm, 1 faces, 0 solids (baked)
FEATURE [Part::Revolution] Revolve023  label="plugHousing044"
  Angle = 360
  Axis = (0,1,0)
  Base = (0,0,0)
  FaceMakerClass = Part::FaceMakerBullseye
  Placement = pos=(0,0,36.15) rot=(0,0,1;0rad)
  Solid = false
  Source = -> Face021
  Symmetric = false
FEATURE [Part::Feature] Face022
  shape: bbox 10 x 16.5 x 2e-07 mm, 1 faces, 0 solids (baked)
FEATURE [Part::Revolution] Revolve018  label="plugHousing032"
  Angle = 360
  Axis = (0,1,0)
  Base = (0,0,0)
  FaceMakerClass = Part::FaceMakerBullseye
  Placement = pos=(0,0,36.15) rot=(0,0,1;0rad)
  Solid = false
  Source = -> Face022
  Symmetric = false
FEATURE [Part::MultiFuse] Fusion022  label="plugHousing040"
  Placement = pos=(0,0,0) rot=(0,0,1;1.5708rad)
  Shapes = -> [Revolve018,Revolve023]
FEATURE [Part::Feature] Face023
  shape: bbox 10 x 16.5 x 2e-07 mm, 1 faces, 0 solids (baked)
FEATURE [Part::Revolution] Revolve021  label="plugHousing035"
  Angle = 360
  Axis = (0,1,0)
  Base = (0,0,0)
  FaceMakerClass = Part::FaceMakerBullseye
  Placement = pos=(0,0,36.15) rot=(0,0,1;0rad)
  Solid = false
  Source = -> Face023
  Symmetric = false
FEATURE [Part::MultiFuse] Fusion018  label="plugHousing036"
  Placement = pos=(0,0,0) rot=(0,0,1;1.5708rad)
  Shapes = -> [Revolve022,Revolve021]
FEATURE [Part::MultiFuse] Fusion019  label="plugHousing037"
  Placement = pos=(0,19,0) rot=(0,0,1;3.14159rad)
  Shapes = -> [Fusion018,Fusion022]
FEATURE [Part::MultiFuse] Fusion024  label="plugHousing042"
  Placement = pos=(122.621,0,-0.15) rot=(0,0,1;0rad)
  Shapes = -> [Fusion023,Fusion019]
FEATURE [Part::Cylinder] Cylinder006
  Angle = 360
  AttacherType = Attacher::AttachEngine3D
  Height = 20
  Placement = pos=(0,0,36.15) rot=(0,0,1;0rad)
  Radius = 14.3
FEATURE [Part::Cylinder] Cylinder007
  Angle = 360
  AttacherType = Attacher::AttachEngine3D
  Height = 10
  Placement = pos=(0,0,36.15) rot=(0,0,1;0rad)
  Radius = 4
FEATURE [Part::MultiFuse] Fusion026  label="removeToCreteHoleForPlugHousing"
  Placement = pos=(70,19,36) rot=(0,1,0;1.5708rad)
  Shapes = -> [Cylinder006,Cylinder007]
FEATURE [Part::Box] Box001  label="Cube001"
  AttacherType = Attacher::AttachEngine3D
  Height = 28
  Length = 3
  Placement = pos=(110.7,19,22) rot=(0,0,1;0rad)
  Width = 15.7
FEATURE [Part::Cut] Cut003  label="top002"
  Base = -> Cut001
  Tool = -> Fusion007
FEATURE [Part::Revolution] Revolve008  label="plugHousing015"
  Angle = 360
  Axis = (0,1,0)
  Base = (0,0,0)
  FaceMakerClass = Part::FaceMakerBullseye
  Placement = pos=(0,0,36.15) rot=(0,0,1;0rad)
  Solid = false
  Source = -> Face010
  Symmetric = false
FEATURE [Part::MultiFuse] Fusion014  label="plugHousing023"
  Placement = pos=(0,0,0) rot=(0,0,1;1.5708rad)
  Shapes = -> [Revolve011,Revolve009]
FEATURE [Part::MultiFuse] Fusion013  label="plugHousing020"
  Placement = pos=(0,0,0) rot=(0,0,1;1.5708rad)
  Shapes = -> [Revolve008,Revolve012]
FEATURE [Part::MultiFuse] Fusion016  label="plugHousing028"
  Placement = pos=(0,19,0) rot=(0,0,1;3.14159rad)
  Shapes = -> [Fusion014,Fusion013]
FEATURE [Part::MultiFuse] Fusion017  label="plugHousing029"
  Placement = pos=(122.621,0,-0.15) rot=(0,0,1;0rad)
  Shapes = -> [Fusion016,Fusion012]
FEATURE [Part::Cut] Cut004  label="top003"
  Base = -> Cut003
  Placement = pos=(1,0,0) rot=(0,0,1;0rad)
  Tool = -> Fusion026
FEATURE [Part::Cylinder] Cylinder008
  Angle = 360
  AttacherType = Attacher::AttachEngine3D
  Height = 20
  Placement = pos=(0,0,36.15) rot=(0,0,1;0rad)
  Radius = 10.3
FEATURE [Part::Cylinder] Cylinder009
  Angle = 360
  AttacherType = Attacher::AttachEngine3D
  Height = 10
  Placement = pos=(0,0,36.15) rot=(0,0,1;0rad)
  Radius = 4
FEATURE [Part::MultiFuse] Fusion027  label="removeToCreteHoleForPlugHousing001"
  Placement = pos=(70,19,36) rot=(0,1,0;1.5708rad)
  Shapes = -> [Cylinder008,Cylinder009]
FEATURE [Part::Cut] Cut005  label="plugHousingTab"
  Base = -> Box001
  Tool = -> Fusion027
FEATURE [Part::MultiFuse] Fusion028  label="plugHousing045"
  Shapes = -> [Fusion024,Cut005]
FEATURE [Part::Box] Box002  label="Cube002"
  AttacherType = Attacher::AttachEngine3D
  Height = 28.8
  Length = 3
  Placement = pos=(107.3,28,21.6) rot=(0,0,1;0rad)
  Width = 7
FEATURE [Part::Box] Box003  label="Cube003"
  AttacherType = Attacher::AttachEngine3D
  Height = 3
  Length = 6.4
  Placement = pos=(107.3,28,18.6) rot=(0,0,1;0rad)
  Width = 7
FEATURE [Part::Box] Box004  label="Cube004"
  AttacherType = Attacher::AttachEngine3D
  Height = 3
  Length = 6.4
  Placement = pos=(107.3,28,50.4) rot=(0,0,1;0rad)
  Width = 7
FEATURE [Part::MultiFuse] Fusion029  label="plugHousingBracketHolder"
  Shapes = -> [Box004,Box002,Box003]
FEATURE [Part::Cylinder] Cylinder010
  Angle = 360
  AttacherType = Attacher::AttachEngine3D
  Height = 20
  Placement = pos=(0,0,36.15) rot=(0,0,1;0rad)
  Radius = 14.3
FEATURE [Part::Cylinder] Cylinder011
  Angle = 360
  AttacherType = Attacher::AttachEngine3D
  Height = 10
  Placement = pos=(0,0,36.15) rot=(0,0,1;0rad)
  Radius = 4
FEATURE [Part::MultiFuse] Fusion030  label="removeToCreteHoleForPlugHousing002"
  Placement = pos=(70,19,36) rot=(0,1,0;1.5708rad)
  Shapes = -> [Cylinder010,Cylinder011]
FEATURE [Part::Cut] Cut006  label="plugHousingBracketHolder001"
  Base = -> Fusion029
  Tool = -> Fusion030
FEATURE [Part::Cylinder] Cylinder012
  Angle = 360
  AttacherType = Attacher::AttachEngine3D
  Height = 20
  Placement = pos=(0,0,36.15) rot=(0,0,1;0rad)
  Radius = 7
FEATURE [Part::Cylinder] Cylinder013
  Angle = 360
  AttacherType = Attacher::AttachEngine3D
  Height = 10
  Placement = pos=(0,0,36.15) rot=(0,0,1;0rad)
  Radius = 4
FEATURE [Part::MultiFuse] Fusion032  label="removeToCreteHoleForPlugHousing003"
  Placement = pos=(70,19,36) rot=(0,1,0;1.5708rad)
  Shapes = -> [Cylinder012,Cylinder013]
FEATURE [Part::Cut] Cut007  label="bottom002"
  Base = -> Cut002
  Tool = -> Fusion032
FEATURE [Sketcher::SketchObject] Sketch008
  FullyConstrained = true
  sketch-geometry (54):
    g0: LineSegment StartX=-4.2 StartY=0 StartZ=0 EndX=-6.2 EndY=0 EndZ=0
    g1: LineSegment StartX=-14 StartY=-18 StartZ=0 EndX=-14 EndY=-26.5 EndZ=0
    g2: LineSegment StartX=-4.2 StartY=0 StartZ=0 EndX=-4.2 EndY=-13.4877 EndZ=0
    g3: Circle CenterX=-4.2 CenterY=-13.4877 CenterZ=0 NormalX=0 NormalY=0 NormalZ=1 AngleXU=0 Radius=1
    g4: Circle CenterX=-4.2 CenterY=-26.5 CenterZ=0 NormalX=0 NormalY=0 NormalZ=1 AngleXU=0 Radius=1
    g5: Circle CenterX=-8.2 CenterY=-26.5 CenterZ=0 NormalX=0 NormalY=0 NormalZ=1 AngleXU=0 Radius=1
    g6: BSplineCurve PolesCount=3 KnotsCount=2 Degree=2 IsPeriodic=0
    g7: GeomPoint X=-4.2 Y=-13.4877 Z=0
    g8: GeomPoint X=-8.2 Y=-26.5 Z=0
    g9: LineSegment StartX=-14 StartY=-26.5 StartZ=0 EndX=-8.2 EndY=-26.5 EndZ=0
    g10: LineSegment StartX=-10.15 StartY=-12 StartZ=0 EndX=-10.15 EndY=-14 EndZ=0
    g11: LineSegment StartX=-12.8401 StartY=-16 StartZ=0 EndX=-10.1571 EndY=-16 EndZ=0
    g12: LineSegment StartX=-10.15 StartY=-14 StartZ=0 EndX=-8.70761 EndY=-14 EndZ=0
    g13: LineSegment StartX=-12.8401 StartY=-16 StartZ=0 EndX=-12.8401 EndY=-17.6958 EndZ=0
    g14: LineSegment StartX=-10.15 StartY=-12 StartZ=0 EndX=-7.79258 EndY=-12 EndZ=0
    g15: Circle CenterX=-6.2215 CenterY=-2 CenterZ=0 NormalX=0 NormalY=0 NormalZ=1 AngleXU=0 Radius=1
    g16: Circle CenterX=-6.22762 CenterY=-2.58724 CenterZ=0 NormalX=0 NormalY=0 NormalZ=1 AngleXU=0 Radius=1
    g17: Circle CenterX=-6.32538 CenterY=-4 CenterZ=0 NormalX=0 NormalY=0 NormalZ=1 AngleXU=0 Radius=1
    g18: BSplineCurve PolesCount=3 KnotsCount=2 Degree=2 IsPeriodic=0
    g19: GeomPoint X=-6.2215 Y=-2 Z=0
    g20: GeomPoint X=-6.32538 Y=-4 Z=0
    g21: Circle CenterX=-6.48644 CenterY=-5.99526 CenterZ=0 NormalX=0 NormalY=0 NormalZ=1 AngleXU=0 Radius=1
    g22: Circle CenterX=-6.58486 CenterY=-6.99526 CenterZ=0 NormalX=0 NormalY=0 NormalZ=1 AngleXU=0 Radius=1
    g23: Circle CenterX=-6.77343 CenterY=-8 CenterZ=0 NormalX=0 NormalY=0 NormalZ=1 AngleXU=0 Radius=1
    g24: BSplineCurve PolesCount=3 KnotsCount=2 Degree=2 IsPeriodic=0
    g25: GeomPoint X=-6.48644 Y=-5.99526 Z=0
    g26: GeomPoint X=-6.77343 Y=-8 Z=0
    g27: Circle CenterX=-7.19003 CenterY=-10 CenterZ=0 NormalX=0 NormalY=0 NormalZ=1 AngleXU=0 Radius=1
    g28: Circle CenterX=-7.44407 CenterY=-11.0915 CenterZ=0 NormalX=0 NormalY=0 NormalZ=1 AngleXU=0 Radius=1
    g29: Circle CenterX=-7.79258 CenterY=-12 CenterZ=0 NormalX=0 NormalY=0 NormalZ=1 AngleXU=0 Radius=1
    g30: BSplineCurve PolesCount=3 KnotsCount=2 Degree=2 IsPeriodic=0
    g31: GeomPoint X=-7.19003 Y=-10 Z=0
    g32: GeomPoint X=-7.79258 Y=-12 Z=0
    g33: Circle CenterX=-8.70761 CenterY=-14 CenterZ=0 NormalX=0 NormalY=0 NormalZ=1 AngleXU=0 Radius=1
    g34: Circle CenterX=-9.33087 CenterY=-15.1837 CenterZ=0 NormalX=0 NormalY=0 NormalZ=1 AngleXU=0 Radius=1
    g35: Circle CenterX=-10.1571 CenterY=-16 CenterZ=0 NormalX=0 NormalY=0 NormalZ=1 AngleXU=0 Radius=1
    g36: BSplineCurve PolesCount=3 KnotsCount=2 Degree=2 IsPeriodic=0
    g37: GeomPoint X=-8.70761 Y=-14 Z=0
    g38: GeomPoint X=-10.1571 Y=-16 Z=0
    g39: Circle CenterX=-12.8401 CenterY=-17.6958 CenterZ=0 NormalX=0 NormalY=0 NormalZ=1 AngleXU=0 Radius=1
    g40: Circle CenterX=-13.3521 CenterY=-17.9027 CenterZ=0 NormalX=0 NormalY=0 NormalZ=1 AngleXU=0 Radius=1
    g41: Circle CenterX=-14 CenterY=-18 CenterZ=0 NormalX=0 NormalY=0 NormalZ=1 AngleXU=0 Radius=1
    g42: BSplineCurve PolesCount=3 KnotsCount=2 Degree=2 IsPeriodic=0
    g43: GeomPoint X=-12.8401 Y=-17.6958 Z=0
    g44: GeomPoint X=-14 Y=-18 Z=0
    g45: LineSegment StartX=-6.2 StartY=0 StartZ=0 EndX=-7.2 EndY=0 EndZ=0
    g46: LineSegment StartX=-7.2 StartY=0 StartZ=0 EndX=-7.2 EndY=-2 EndZ=0
    g47: LineSegment StartX=-7.2 StartY=-2 StartZ=0 EndX=-6.2215 EndY=-2 EndZ=0
    g48: LineSegment StartX=-6.32538 StartY=-4 StartZ=0 EndX=-7.65538 EndY=-4 EndZ=0
    g49: LineSegment StartX=-7.65538 StartY=-4 StartZ=0 EndX=-7.65538 EndY=-5.99526 EndZ=0
    g50: LineSegment StartX=-7.65538 StartY=-5.99526 StartZ=0 EndX=-6.48644 EndY=-5.99526 EndZ=0
    g51: LineSegment StartX=-6.77343 StartY=-8 StartZ=0 EndX=-8.43343 EndY=-8 EndZ=0
    g52: LineSegment StartX=-8.43343 StartY=-8 StartZ=0 EndX=-8.43343 EndY=-10 EndZ=0
    g53: LineSegment StartX=-8.43343 StartY=-10 StartZ=0 EndX=-7.19003 EndY=-10 EndZ=0
  constraints (112):
    c: Horizontal(g0)
    c: Distance(g0) = 2
    c: Block(g0)
    c: Vertical(g1)
    c: Coincident(g2,g0)
    c: Vertical(g2)
    c: Block(g2)
    c: Coincident(g6,g2)
    c: Weight(g3) = 1
    c: Equal(g3,g4)
    c: Equal(g3,g5)
    c: InternalAlignment(g3,g6)
    c: InternalAlignment(g4,g6)
    c: InternalAlignment(g5,g6)
    c: InternalAlignment(g7,g6)
    c: InternalAlignment(g8,g6)
    c: Block(g6)
    c: Coincident(g9,g1)
    c: Coincident(g9,g6)
    c: Horizontal(g9)
    c: Vertical(g10)
    c: Block(g10)
    c: Horizontal(g11)
    c: Block(g11)
    c: Coincident(g12,g10)
    c: Horizontal(g12)
    c: Block(g12)
    c: Coincident(g13,g11)
    c: Vertical(g13)
    c: Block(g13)
    c: Coincident(g14,g10)
    c: Horizontal(g14)
    c: Block(g14)
    c: Block(g9)
    c: Block(g1)
    c: Weight(g15) = 1
    c: Equal(g15,g16)
    c: Equal(g15,g17)
    c: InternalAlignment(g15,g18)
    c: InternalAlignment(g16,g18)
    c: InternalAlignment(g17,g18)
    c: InternalAlignment(g19,g18)
    c: InternalAlignment(g20,g18)
    c: Weight(g21) = 1
    c: Equal(g21,g22)
    c: Equal(g21,g23)
    c: InternalAlignment(g21,g24)
    c: InternalAlignment(g22,g24)
    c: InternalAlignment(g23,g24)
    c: InternalAlignment(g25,g24)
    c: InternalAlignment(g26,g24)
    c: Weight(g27) = 1
    c: Equal(g27,g28)
    c: Equal(g27,g29)
    c: Coincident(g30,g14)
    c: InternalAlignment(g27,g30)
    c: InternalAlignment(g28,g30)
    c: InternalAlignment(g29,g30)
    c: InternalAlignment(g31,g30)
    c: InternalAlignment(g32,g30)
    c: Coincident(g36,g12)
    c: Weight(g33) = 1
    c: Equal(g33,g34)
    c: Equal(g33,g35)
    c: Coincident(g36,g11)
    c: InternalAlignment(g33,g36)
    c: InternalAlignment(g34,g36)
    c: InternalAlignment(g35,g36)
    c: InternalAlignment(g37,g36)
    c: InternalAlignment(g38,g36)
    c: Coincident(g42,g13)
    c: Weight(g39) = 1
    c: Equal(g39,g40)
    c: Equal(g39,g41)
    c: Coincident(g42,g1)
    c: InternalAlignment(g39,g42)
    c: InternalAlignment(g40,g42)
    c: InternalAlignment(g41,g42)
    c: InternalAlignment(g43,g42)
    c: InternalAlignment(g44,g42)
    c: Block(g18)
    c: Block(g24)
    c: Block(g30)
    c: Block(g36)
    c: Block(g42)
    c: Horizontal(g45)
    c: Coincident(g45,g0)
    c: Vertical(g46)
    c: Coincident(g46,g45)
    c: Coincident(g47,g46)
    c: Coincident(g47,g18)
    c: Horizontal(g47)
    c: Block(g46)
    c: Coincident(g48,g18)
    c: Horizontal(g48)
    c: Distance(g48) = 1.33
    c: Vertical(g49)
    c: Coincident(g49,g48)
    c: Coincident(g50,g49)
    c: Coincident(g50,g24)
    c: Horizontal(g50)
    c: Tangent(g50,g22)
    c: Horizontal(g51)
    c: Coincident(g51,g24)
    c: Block(g51)
    c: Vertical(g52)
    c: Block(g52)
    c: Coincident(g52,g51)
    c: Coincident(g53,g52)
    c: Coincident(g53,g30)
    c: Horizontal(g53)
    c: Distance(g1) = 8.5
FEATURE [Part::Feature] Face024
  shape: bbox 9.8 x 26.5 x 2e-07 mm, 1 faces, 0 solids (baked)
FEATURE [Part::Revolution] Revolve024
  Angle = 360
  Axis = (0,1,0)
  Base = (0,0,0)
  FaceMakerClass = Part::FaceMakerBullseye
  Placement = pos=(0,0,0) rot=(0,0,1;1.5708rad)
  Solid = false
  Source = -> Face024
  Symmetric = false
FEATURE [Part::Feature] Face025
  shape: bbox 9.8 x 26.5 x 2e-07 mm, 1 faces, 0 solids (baked)
FEATURE [Part::Revolution] Revolve025
  Angle = 360
  Axis = (0,1,0)
  Base = (0,0,0)
  FaceMakerClass = Part::FaceMakerBullseye
  Placement = pos=(0,0,0) rot=(0,0,1;1.5708rad)
  Solid = false
  Source = -> Face025
  Symmetric = false
FEATURE [Part::MultiFuse] Fusion033
  Placement = pos=(-18,19,36) rot=(0,0,1;0rad)
  Shapes = -> [Revolve025,Revolve024]
FEATURE [Part::Cylinder] Cylinder014
  Angle = 360
  AttacherType = Attacher::AttachEngine3D
  Height = 20
  Placement = pos=(0,0,36.15) rot=(0,0,1;0rad)
  Radius = 14.3
FEATURE [Part::Cylinder] Cylinder015
  Angle = 360
  AttacherType = Attacher::AttachEngine3D
  Height = 10
  Placement = pos=(0,0,36.15) rot=(0,0,1;0rad)
  Radius = 4
FEATURE [Part::MultiFuse] Fusion034  label="removeToCreteHoleForPlugHousing004"
  Placement = pos=(-42,19,36) rot=(0,1,0;1.5708rad)
  Shapes = -> [Cylinder014,Cylinder015]
FEATURE [Part::Cut] Cut008  label="top004"
  Base = -> Cut004
  Placement = pos=(-1,0,0) rot=(0,0,1;0rad)
  Tool = -> Fusion034
FEATURE [Part::Box] Box005  label="Cube005"
  AttacherType = Attacher::AttachEngine3D
  Height = 28
  Length = 3
  Placement = pos=(110.7,19,22) rot=(0,0,1;0rad)
  Width = 15.7
FEATURE [Part::Cylinder] Cylinder016
  Angle = 360
  AttacherType = Attacher::AttachEngine3D
  Height = 10
  Placement = pos=(0,0,36.15) rot=(0,0,1;0rad)
  Radius = 4
FEATURE [Part::Cylinder] Cylinder017
  Angle = 360
  AttacherType = Attacher::AttachEngine3D
  Height = 20
  Placement = pos=(0,0,36.15) rot=(0,0,1;0rad)
  Radius = 10.3
FEATURE [Part::MultiFuse] Fusion035  label="removeToCreteHoleForPlugHousing005"
  Placement = pos=(70,19,36) rot=(0,1,0;1.5708rad)
  Shapes = -> [Cylinder017,Cylinder016]
FEATURE [Part::Cut] Cut009  label="plugHousingTab001"
  Base = -> Box005
  Placement = pos=(-107.4,-14,0) rot=(0,0,1;0rad)
  Tool = -> Fusion035
FEATURE [Part::Box] Box006  label="Cube006"
  AttacherType = Attacher::AttachEngine3D
  Height = 28
  Length = 3
  Placement = pos=(110.7,19,22) rot=(0,0,1;0rad)
  Width = 15.7
FEATURE [Part::Cylinder] Cylinder018
  Angle = 360
  AttacherType = Attacher::AttachEngine3D
  Height = 10
  Placement = pos=(0,0,36.15) rot=(0,0,1;0rad)
  Radius = 4
FEATURE [Part::Cylinder] Cylinder019
  Angle = 360
  AttacherType = Attacher::AttachEngine3D
  Height = 20
  Placement = pos=(0,0,36.15) rot=(0,0,1;0rad)
  Radius = 10.3
FEATURE [Part::MultiFuse] Fusion036  label="removeToCreteHoleForPlugHousing006"
  Placement = pos=(70,19,36) rot=(0,1,0;1.5708rad)
  Shapes = -> [Cylinder019,Cylinder018]
FEATURE [Part::Cut] Cut010  label="plugHousingTab002"
  Base = -> Box006
  Placement = pos=(-107.4,-14,0) rot=(0,0,1;0rad)
  Tool = -> Fusion036
FEATURE [Part::MultiFuse] Fusion037
  Placement = pos=(9.6,23,0) rot=(0,0,1;3.14159rad)
  Shapes = -> [Cut009,Cut010]
FEATURE [Part::Box] Box  label="Cube"
  AttacherType = Attacher::AttachEngine3D
  Height = 10
  Length = 3
  Placement = pos=(3.3,4,12) rot=(0,0,1;0rad)
  Width = 10
FEATURE [Part::Fillet] Fillet004
  Base = -> Fusion028
  Edges = 1 edges r=2: [Edge25]
FEATURE [Part::Fillet] Fillet005  label="plugHousing046"
  Base = -> Fillet004
  Edges = 1 edges r=2: [Edge8]
FEATURE [Part::Fillet] Fillet006
  Base = -> Box
  Edges = 1 edges r=2: [Edge11]
FEATURE [Part::Box] Box007  label="Cube007"
  AttacherType = Attacher::AttachEngine3D
  Height = 10
  Length = 3
  Placement = pos=(3.3,4,50) rot=(0,0,1;0rad)
  Width = 10
FEATURE [Part::Fillet] Fillet007
  Base = -> Box007
  Edges = 1 edges r=2: [Edge12]
FEATURE [Part::Box] Box008  label="Cube008"
  AttacherType = Attacher::AttachEngine3D
  Height = 28
  Length = 4
  Placement = pos=(5,0,22) rot=(0,0,1;0rad)
  Width = 10
FEATURE [Part::Fillet] Fillet008
  Base = -> Box008
  Edges = 1 edges r=1: [Edge7]
FEATURE [Part::Fillet] Fillet009
  Base = -> Fillet008
  Edges = 1 edges r=2: [Edge5]
FEATURE [Part::Fillet] Fillet010
  Base = -> Fillet009
  Edges = 1 edges r=2: [Edge2]
FEATURE [Sketcher::SketchObject] Sketch009  label="topSketch003"
  FullyConstrained = true
  sketch-geometry (4):
    g0: LineSegment StartX=16.8446 StartY=31.512 StartZ=0 EndX=16.3251 EndY=34.4666 EndZ=0
    g1: ArcOfCircle CenterX=19 CenterY=19.2524 CenterZ=0 NormalX=0 NormalY=0 NormalZ=1 AngleXU=0 Radius=15.4476 StartAngle=1.74483 EndAngle=2.72717
    g2: ArcOfCircle CenterX=19 CenterY=19.2524 CenterZ=0 NormalX=0 NormalY=0 NormalZ=1 AngleXU=0 Radius=12.4476 StartAngle=1.74483 EndAngle=2.73189
    g3: LineSegment StartX=4.86004 StartY=25.4725 StartZ=0 EndX=7.58253 EndY=24.2107 EndZ=0
  constraints (7):
    c: Block(g0)
    c: Coincident(g1,g0)
    c: Coincident(g2,g0)
    c: Coincident(g3,g1)
    c: Coincident(g3,g2)
    c: Block(g1)
    c: Block(g2)
FEATURE [Part::Extrusion] Extrude008
  Base = -> Sketch009
  Dir = (0,0,1)
  DirMode = 2
  FaceMakerClass = Part::FaceMakerBullseye
  LengthFwd = 10
  LengthRev = 0
  Placement = pos=(0,0,31) rot=(0,0,1;0rad)
  Solid = true
  Symmetric = false
FEATURE [Part::Cylinder] Cylinder020
  Angle = 360
  AttacherType = Attacher::AttachEngine3D
  Height = 20
  Placement = pos=(0,0,36.15) rot=(0,0,1;0rad)
  Radius = 8.2
FEATURE [Part::Cylinder] Cylinder021
  Angle = 360
  AttacherType = Attacher::AttachEngine3D
  Height = 10
  Placement = pos=(0,0,36.15) rot=(0,0,1;0rad)
  Radius = 4
FEATURE [Part::MultiFuse] Fusion038  label="removeToCreteHoleForPlugHousing007"
  Placement = pos=(-42,19,36) rot=(0,1,0;1.5708rad)
  Shapes = -> [Cylinder020,Cylinder021]
FEATURE [Part::Cut] Cut011
  Base = -> Extrude008
  Tool = -> Fusion038
FEATURE [Part::Fillet] Fillet011
  Base = -> Cut011
  Edges = 1 edges r=2: [Edge1]
FEATURE [Part::Fillet] Fillet012
  Base = -> Fillet011
  Edges = 1 edges r=2.5: [Edge1]
FEATURE [Part::Fillet] Fillet013
  Base = -> Fillet012
  Edges = 1 edges r=2.5: [Edge2]
FEATURE [Part::Box] Box010  label="Cube010"
  AttacherType = Attacher::AttachEngine3D
  Height = 16
  Length = 8
  Placement = pos=(12.7,31.52,28) rot=(0,0,1;0rad)
  Width = 4
FEATURE [Sketcher::SketchObject] Sketch010  label="topSketch004"
  FullyConstrained = true
  sketch-geometry (4):
    g0: LineSegment StartX=16.8446 StartY=31.512 StartZ=0 EndX=16.3251 EndY=34.4666 EndZ=0
    g1: ArcOfCircle CenterX=19 CenterY=19.2524 CenterZ=0 NormalX=0 NormalY=0 NormalZ=1 AngleXU=0 Radius=15.4476 StartAngle=1.74483 EndAngle=2.72717
    g2: ArcOfCircle CenterX=19 CenterY=19.2524 CenterZ=0 NormalX=0 NormalY=0 NormalZ=1 AngleXU=0 Radius=12.4476 StartAngle=1.74483 EndAngle=2.73189
    g3: LineSegment StartX=4.86004 StartY=25.4725 StartZ=0 EndX=7.58253 EndY=24.2107 EndZ=0
  constraints (7):
    c: Block(g0)
    c: Coincident(g1,g0)
    c: Coincident(g2,g0)
    c: Coincident(g3,g1)
    c: Coincident(g3,g2)
    c: Block(g1)
    c: Block(g2)
FEATURE [Part::Cylinder] Cylinder022
  Angle = 360
  AttacherType = Attacher::AttachEngine3D
  Height = 10
  Placement = pos=(0,0,36.15) rot=(0,0,1;0rad)
  Radius = 4
FEATURE [Sketcher::SketchObject] Sketch011  label="topSketch005"
  FullyConstrained = true
  sketch-geometry (4):
    g0: LineSegment StartX=16.8446 StartY=31.512 StartZ=0 EndX=16.3251 EndY=34.4666 EndZ=0
    g1: ArcOfCircle CenterX=19 CenterY=19.2524 CenterZ=0 NormalX=0 NormalY=0 NormalZ=1 AngleXU=0 Radius=15.4476 StartAngle=1.74483 EndAngle=2.72717
    g2: ArcOfCircle CenterX=19 CenterY=19.2524 CenterZ=0 NormalX=0 NormalY=0 NormalZ=1 AngleXU=0 Radius=12.4476 StartAngle=1.74483 EndAngle=2.73189
    g3: LineSegment StartX=4.86004 StartY=25.4725 StartZ=0 EndX=7.58253 EndY=24.2107 EndZ=0
  constraints (7):
    c: Block(g0)
    c: Coincident(g1,g0)
    c: Coincident(g2,g0)
    c: Coincident(g3,g1)
    c: Coincident(g3,g2)
    c: Block(g1)
    c: Block(g2)
FEATURE [Part::Extrusion] Extrude010
  Base = -> Sketch011
  Dir = (0,0,1)
  DirMode = 2
  FaceMakerClass = Part::FaceMakerBullseye
  LengthFwd = 10.6
  LengthRev = 0
  Placement = pos=(0,0,31) rot=(0,0,1;0rad)
  Solid = true
  Symmetric = false
FEATURE [Part::Cylinder] Cylinder023
  Angle = 360
  AttacherType = Attacher::AttachEngine3D
  Height = 20
  Placement = pos=(0,0,36.15) rot=(0,0,1;0rad)
  Radius = 8.2
FEATURE [Part::MultiFuse] Fusion039  label="removeToCreteHoleForPlugHousing008"
  Placement = pos=(-42,19,36) rot=(0,1,0;1.5708rad)
  Shapes = -> [Cylinder023,Cylinder022]
FEATURE [Part::Cut] Cut012
  Base = -> Extrude010
  Placement = pos=(0,0,-0.3) rot=(0,0,1;0rad)
  Tool = -> Fusion039
FEATURE [Part::Cut] Cut013
  Base = -> Box010
  Tool = -> Cut012
FEATURE [Part::Fillet] Fillet014
  Base = -> Cut013
  Edges = 1 edges r=0.7: [Edge13]
FEATURE [Part::Fillet] Fillet015
  Base = -> Fillet014
  Edges = 1 edges r=0.7: [Edge13]
FEATURE [Part::Fillet] Fillet016
  Base = -> Fillet015
  Edges = 1 edges r=0.7: [Edge16]
FEATURE [Part::Fillet] Fillet017
  Base = -> Fillet016
  Edges = 1 edges r=0.7: [Edge11]
FEATURE [Part::Fillet] Fillet018
  Base = -> Fillet017
  Edges = 1 edges r=0.7: [Edge10]
FEATURE [Part::Fillet] Fillet019
  Base = -> Fillet018
  Edges = 1 edges r=1.2: [Edge5]
FEATURE [Part::Fillet] Fillet020
  Base = -> Fillet019
  Edges = 1 edges r=1.2: [Edge12]
FEATURE [Part::Fillet] Fillet021
  Base = -> Fillet020
  Edges = 1 edges r=2: [Edge1]
  Placement = pos=(0.3,0,0) rot=(0,0,1;0rad)
FEATURE [Part::MultiFuse] Fusion040  label="top005"
  Shapes = -> [Cut008,Fillet021]
FEATURE [Part::MultiFuse] Fusion041  label="wireHolder"
  Shapes = -> [Fusion033,Fillet013]
FEATURE [Part::MultiFuse] Fusion042
  Shapes = -> [Fillet007,Fusion041]
FEATURE [Part::MultiFuse] Fusion043  label="wireHolder001"
  Shapes = -> [Fusion042,Fillet010]
FEATURE [Part::MultiFuse] Fusion044  label="wireHolder002"
  Shapes = -> [Fillet006,Fusion037,Fusion043]
FEATURE [Part::Feature] Face026
  shape: bbox 11 x 6 x 2e-07 mm, 1 faces, 0 solids (baked)
FEATURE [Part::Revolution] Revolve026
  Angle = 360
  Axis = (0,1,0)
  Base = (0,0,0)
  FaceMakerClass = Part::FaceMakerBullseye
  Placement = pos=(30.3,-1,19.7) rot=(0,0,1;0rad)
  Solid = false
  Source = -> Face026
  Symmetric = false
FEATURE [Sketcher::SketchObject] Sketch013  label="topSketch006"
  FullyConstrained = true
  sketch-geometry (13):
    g0: LineSegment StartX=117 StartY=19 StartZ=0 EndX=117 EndY=38 EndZ=0
    g1: ArcOfCircle CenterX=98 CenterY=19 CenterZ=0 NormalX=0 NormalY=0 NormalZ=1 AngleXU=0 Radius=19 StartAngle=5.7297 EndAngle=6.28319
    g2: LineSegment StartX=0 StartY=3 StartZ=0 EndX=0 EndY=19 EndZ=0
    g3: LineSegment StartX=19 StartY=38 StartZ=0 EndX=117 EndY=38 EndZ=0
    g4: ArcOfCircle CenterX=19 CenterY=19 CenterZ=0 NormalX=0 NormalY=0 NormalZ=1 AngleXU=0 Radius=19 StartAngle=1.5708 EndAngle=3.14159
    g5: ArcOfCircle CenterX=19 CenterY=19 CenterZ=0 NormalX=0 NormalY=0 NormalZ=1 AngleXU=0 Radius=16 StartAngle=1.5708 EndAngle=3.14159
    g6: ArcOfCircle CenterX=98 CenterY=19 CenterZ=0 NormalX=0 NormalY=0 NormalZ=1 AngleXU=0 Radius=16 StartAngle=5.60905 EndAngle=6.28319
    g7: LineSegment StartX=114 StartY=19 StartZ=0 EndX=114 EndY=35 EndZ=0
    g8: LineSegment StartX=110.5 StartY=9.01251 StartZ=0 EndX=114.163 EndY=9.01251 EndZ=0
    g9: LineSegment StartX=114 StartY=35 StartZ=0 EndX=19 EndY=35 EndZ=0
    g10: LineSegment StartX=0 StartY=3 StartZ=0 EndX=0 EndY=0 EndZ=0
    g11: LineSegment StartX=3 StartY=0 StartZ=0 EndX=0 EndY=0 EndZ=0
    g12: LineSegment StartX=3 StartY=19 StartZ=0 EndX=3 EndY=0 EndZ=0
  constraints (33):
    c: Vertical(g0)
    c: Distance(g0) = 19
    c: Block(g0)
    c: Coincident(g1,g0)
    c: Block(g1)
    c: Vertical(g2)
    c: Block(g2)
    c: Coincident(g3,g0)
    c: Horizontal(g3)
    c: Distance(g3) = 98
    c: Coincident(g4,g3)
    c: Coincident(g4,g2)
    c: Block(g4)
    c: Coincident(g5,g4)
    c: Coincident(g6,g1)
    c: Block(g6)
    c: Block(g5)
    c: Coincident(g7,g6)
    c: Vertical(g7)
    c: Coincident(g8,g6)
    c: Coincident(g8,g1)
    c: Coincident(g9,g7)
    c: Coincident(g9,g5)
    c: Horizontal(g9)
    c: Tangent(g9,g5)
    c: Coincident(g10,g2)
    c: Distance(g10) = 3
    c: Vertical(g10)
    c: Coincident(g11,g10)
    c: Horizontal(g11)
    c: Coincident(g12,g5)
    c: Coincident(g12,g11)
    c: Vertical(g12)
FEATURE [Part::Extrusion] Extrude011  label="top006"
  Base = -> Sketch013
  Dir = (0,0,1)
  DirMode = 2
  FaceMakerClass = Part::FaceMakerBullseye
  LengthFwd = 72
  LengthRev = 0
  Solid = true
  Symmetric = false
FEATURE [Sketcher::SketchObject] Sketch014
  FullyConstrained = true
  MapMode = 3
  Placement = pos=(0,0,0) rot=(1,0,0;1.5708rad)
  Support = -> [Extrude011]
  sketch-geometry (8):
    g0: Circle CenterX=80.351 CenterY=-67.6202 CenterZ=0 NormalX=0 NormalY=0 NormalZ=1 AngleXU=0 Radius=2
    g1: Circle CenterX=80.351 CenterY=-67.6202 CenterZ=0 NormalX=0 NormalY=0 NormalZ=1 AngleXU=0 Radius=3
    g2: Circle CenterX=80.351 CenterY=-4.92017 CenterZ=0 NormalX=0 NormalY=0 NormalZ=1 AngleXU=0 Radius=2
    g3: Circle CenterX=80.351 CenterY=-4.92017 CenterZ=0 NormalX=0 NormalY=0 NormalZ=1 AngleXU=0 Radius=3
    g4: Circle CenterX=23.851 CenterY=-4.92017 CenterZ=0 NormalX=0 NormalY=0 NormalZ=1 AngleXU=0 Radius=2
    g5: Circle CenterX=23.851 CenterY=-4.92017 CenterZ=0 NormalX=0 NormalY=0 NormalZ=1 AngleXU=0 Radius=3
    g6: Circle CenterX=23.851 CenterY=-67.6202 CenterZ=0 NormalX=0 NormalY=0 NormalZ=1 AngleXU=0 Radius=2
    g7: Circle CenterX=23.851 CenterY=-67.6202 CenterZ=0 NormalX=0 NormalY=0 NormalZ=1 AngleXU=0 Radius=3
  constraints (8):
    c: Block(g3)
    c: Block(g2)
    c: Block(g1)
    c: Block(g0)
    c: Block(g6)
    c: Block(g7)
    c: Block(g4)
    c: Block(g5)
FEATURE [Part::Feature] Face027
  shape: bbox 11 x 6 x 2e-07 mm, 1 faces, 0 solids (baked)
FEATURE [Part::Revolution] Revolve027
  Angle = 360
  Axis = (0,1,0)
  Base = (0,0,0)
  FaceMakerClass = Part::FaceMakerBullseye
  Placement = pos=(30.3,-1,51.7) rot=(0,0,1;0rad)
  Solid = false
  Source = -> Face027
  Symmetric = false
FEATURE [Part::Feature] Face028
  shape: bbox 11 x 6 x 2e-07 mm, 1 faces, 0 solids (baked)
FEATURE [Part::Revolution] Revolve028
  Angle = 360
  Axis = (0,1,0)
  Base = (0,0,0)
  FaceMakerClass = Part::FaceMakerBullseye
  Placement = pos=(62.3,-1,19.7) rot=(0,0,1;0rad)
  Solid = false
  Source = -> Face028
  Symmetric = false
FEATURE [Part::Feature] Face029
  shape: bbox 11 x 6 x 2e-07 mm, 1 faces, 0 solids (baked)
FEATURE [Part::Revolution] Revolve029
  Angle = 360
  Axis = (0,1,0)
  Base = (0,0,0)
  FaceMakerClass = Part::FaceMakerBullseye
  Placement = pos=(62.3,-1,51.7) rot=(0,0,1;0rad)
  Solid = false
  Source = -> Face029
  Symmetric = false
FEATURE [Part::Feature] Wire
  shape: bbox 11 x 5.2 x 2e-07 mm, 0 faces, 0 solids (baked)
FEATURE [Part::Revolution] Revolve030
  Angle = 360
  Axis = (0,1,0)
  Base = (0,0,0)
  FaceMakerClass = Part::FaceMakerBullseye
  Placement = pos=(30.3,38,19.7) rot=(0,0,1;0rad)
  Solid = true
  Source = -> Wire
  Symmetric = false
FEATURE [Part::Feature] Wire001
  shape: bbox 11 x 5.2 x 2e-07 mm, 0 faces, 0 solids (baked)
FEATURE [Part::Revolution] Revolve031
  Angle = 360
  Axis = (0,1,0)
  Base = (0,0,0)
  FaceMakerClass = Part::FaceMakerBullseye
  Placement = pos=(30.3,38,51.7) rot=(0,0,1;0rad)
  Solid = true
  Source = -> Wire001
  Symmetric = false
FEATURE [Part::Feature] Wire002
  shape: bbox 11 x 5.2 x 2e-07 mm, 0 faces, 0 solids (baked)
FEATURE [Part::Revolution] Revolve032
  Angle = 360
  Axis = (0,1,0)
  Base = (0,0,0)
  FaceMakerClass = Part::FaceMakerBullseye
  Placement = pos=(62.3,38,51.7) rot=(0,0,1;0rad)
  Solid = true
  Source = -> Wire002
  Symmetric = false
FEATURE [Part::Feature] Wire003
  shape: bbox 11 x 5.2 x 2e-07 mm, 0 faces, 0 solids (baked)
FEATURE [Part::Revolution] Revolve033
  Angle = 360
  Axis = (0,1,0)
  Base = (0,0,0)
  FaceMakerClass = Part::FaceMakerBullseye
  Placement = pos=(62.3,38,19.7) rot=(0,0,1;0rad)
  Solid = true
  Source = -> Wire003
  Symmetric = false
FEATURE [Part::MultiFuse] Fusion045  label="altRandScrewHousing"
  Shapes = -> [Revolve029,Revolve027,Revolve028,Revolve026]
FEATURE [Part::MultiFuse] Fusion046  label="fanScrewHousing"
  Shapes = -> [Revolve033,Revolve032,Revolve031,Revolve030]
FEATURE [Sketcher::SketchObject] Sketch015
  FullyConstrained = true
  sketch-geometry (17):
    g0: Circle CenterX=-3.5 CenterY=23.5 CenterZ=0 NormalX=0 NormalY=0 NormalZ=1 AngleXU=0 Radius=1
    g1: Circle CenterX=-1 CenterY=15.25 CenterZ=0 NormalX=0 NormalY=0 NormalZ=1 AngleXU=0 Radius=1
    g2: Circle CenterX=-3.5 CenterY=7 CenterZ=0 NormalX=0 NormalY=0 NormalZ=1 AngleXU=0 Radius=1
    g3: BSplineCurve PolesCount=3 KnotsCount=2 Degree=2 IsPeriodic=0
    g4: GeomPoint X=-3.5 Y=23.5 Z=0
    g5: GeomPoint X=-3.5 Y=7 Z=0
    g6: Circle CenterX=-4.8 CenterY=30.5 CenterZ=0 NormalX=0 NormalY=0 NormalZ=1 AngleXU=0 Radius=1
    g7: Circle CenterX=-3.5 CenterY=30.5 CenterZ=0 NormalX=0 NormalY=0 NormalZ=1 AngleXU=0 Radius=1
    g8: Circle CenterX=-3.5 CenterY=29.2 CenterZ=0 NormalX=0 NormalY=0 NormalZ=1 AngleXU=0 Radius=1
    g9: BSplineCurve PolesCount=3 KnotsCount=2 Degree=2 IsPeriodic=0
    g10: GeomPoint X=-4.8 Y=30.5 Z=0
    g11: GeomPoint X=-3.5 Y=29.2 Z=0
    g12: LineSegment StartX=-3.5 StartY=29.2 StartZ=0 EndX=-3.5 EndY=23.5 EndZ=0
    g13: LineSegment StartX=-4.8 StartY=30.5 StartZ=0 EndX=0 EndY=30.5 EndZ=0
    g14: LineSegment StartX=-3.5 StartY=0.3 StartZ=0 EndX=0 EndY=0.3 EndZ=0
    g15: LineSegment StartX=-3.5 StartY=0.3 StartZ=0 EndX=-3.5 EndY=7 EndZ=0
    g16: LineSegment StartX=0 StartY=0.3 StartZ=0 EndX=0 EndY=30.5 EndZ=0
  constraints (33):
    c: Weight(g0) = 1
    c: Equal(g0,g1)
    c: Equal(g0,g2)
    c: InternalAlignment(g0,g3)
    c: InternalAlignment(g1,g3)
    c: InternalAlignment(g2,g3)
    c: InternalAlignment(g4,g3)
    c: InternalAlignment(g5,g3)
    c: Block(g3)
    c: Weight(g6) = 1
    c: Equal(g6,g7)
    c: Equal(g6,g8)
    c: InternalAlignment(g6,g9)
    c: InternalAlignment(g7,g9)
    c: InternalAlignment(g8,g9)
    c: InternalAlignment(g10,g9)
    c: InternalAlignment(g11,g9)
    c: Block(g9)
    c: Coincident(g12,g9)
    c: Coincident(g12,g3)
    c: Vertical(g12)
    c: Coincident(g13,g9)
    c: Horizontal(g13)
    c: Distance(g13) = 4.8
    c: Horizontal(g14)
    c: Block(g14)
    c: Coincident(g15,g14)
    c: Coincident(g15,g3)
    c: Vertical(g15)
    c: Coincident(g16,g14)
    c: Coincident(g16,g13)
    c: Vertical(g16)
    c: Tangent(g16,g1)
FEATURE [Sketcher::SketchObject] Sketch016
  FullyConstrained = true
  sketch-geometry (15):
    g0: LineSegment StartX=0 StartY=0 StartZ=0 EndX=-3.5 EndY=0 EndZ=0
    g1: LineSegment StartX=-3.5 StartY=0 StartZ=0 EndX=-3.5 EndY=7 EndZ=0
    g2: Circle CenterX=-3.5 CenterY=23.5 CenterZ=0 NormalX=0 NormalY=0 NormalZ=1 AngleXU=0 Radius=1
    g3: Circle CenterX=-1 CenterY=15.25 CenterZ=0 NormalX=0 NormalY=0 NormalZ=1 AngleXU=0 Radius=1
    g4: Circle CenterX=-3.5 CenterY=7 CenterZ=0 NormalX=0 NormalY=0 NormalZ=1 AngleXU=0 Radius=1
    g5: BSplineCurve PolesCount=3 KnotsCount=2 Degree=2 IsPeriodic=0
    g6: GeomPoint X=-3.5 Y=23.5 Z=0
    g7: GeomPoint X=-3.5 Y=7 Z=0
    g8: LineSegment StartX=-3.5 StartY=28.2 StartZ=0 EndX=-3.5 EndY=23.5 EndZ=0
    g9: LineSegment StartX=0 StartY=0 StartZ=0 EndX=0 EndY=29.5 EndZ=0
    g10: LineSegment StartX=0 StartY=29.5 StartZ=0 EndX=0 EndY=30 EndZ=0
    g11: LineSegment StartX=-3.5 StartY=28.2 StartZ=0 EndX=-3.5 EndY=30 EndZ=0
    g12: LineSegment StartX=0 StartY=30 StartZ=0 EndX=0 EndY=30.5 EndZ=0
    g13: LineSegment StartX=0 StartY=30.5 StartZ=0 EndX=-3.5 EndY=30.5 EndZ=0
    g14: LineSegment StartX=-3.5 StartY=30.5 StartZ=0 EndX=-3.5 EndY=30 EndZ=0
  constraints (38):
    c: Coincident(g0,g-1)
    c: Horizontal(g0)
    c: Distance(g0) = 3.5
    c: Coincident(g1,g0)
    c: Vertical(g1)
    c: Distance(g1) = 7
    c: Weight(g2) = 1
    c: Equal(g2,g3)
    c: Equal(g2,g4)
    c: Coincident(g5,g1)
    c: InternalAlignment(g2,g5)
    c: InternalAlignment(g3,g5)
    c: InternalAlignment(g4,g5)
    c: InternalAlignment(g6,g5)
    c: InternalAlignment(g7,g5)
    c: Block(g5)
    c: Coincident(g8,g5)
    c: Vertical(g8)
    c: Coincident(g9,g0)
    c: Vertical(g9)
    c: Tangent(g9,g3)
    c: Vertical(g10)
    c: Distance(g10) = 0.5
    c: Coincident(g11,g8)
    c: Vertical(g11)
    c: Block(g9)
    c: Block(g8)
    c: Block(g10)
    c: Vertical(g12)
    c: Equal(g10,g12) = 0.5
    c: Block(g12)
    c: Coincident(g12,g10)
    c: Horizontal(g13)
    c: Coincident(g13,g12)
    c: Coincident(g14,g13)
    c: Coincident(g14,g11)
    c: Vertical(g14)
    c: Block(g14)
FEATURE [Part::Feature] Face032
  shape: bbox 3.5 x 30.5 x 2e-07 mm, 1 faces, 0 solids (baked)
FEATURE [Part::Revolution] Revolve036  label="backCaseScrewPost001"
  Angle = 360
  Axis = (0,1,0)
  Base = (0,0,0)
  FaceMakerClass = Part::FaceMakerBullseye
  Placement = pos=(12.5,4.5,10) rot=(0,0,1;0rad)
  Solid = false
  Source = -> Face032
  Symmetric = false
FEATURE [Part::Feature] Face033
  shape: bbox 3.5 x 30.5 x 2e-07 mm, 1 faces, 0 solids (baked)
FEATURE [Sketcher::SketchObject] Sketch017
  FullyConstrained = true
  sketch-geometry (11):
    g0: LineSegment StartX=-3.5 StartY=1e-16 StartZ=0 EndX=-1.6 EndY=1e-16 EndZ=0
    g1: LineSegment StartX=-1.6 StartY=1e-16 StartZ=0 EndX=-1.6 EndY=1.5 EndZ=0
    g2: LineSegment StartX=-3.5 StartY=1.5 StartZ=0 EndX=-1.6 EndY=1.5 EndZ=0
    g3: LineSegment StartX=-3.5 StartY=1e-16 StartZ=0 EndX=-4.8 EndY=1e-16 EndZ=0
    g4: Circle CenterX=-3.5 CenterY=1.3 CenterZ=0 NormalX=0 NormalY=0 NormalZ=1 AngleXU=0 Radius=1
    g5: Circle CenterX=-3.5 CenterY=1e-16 CenterZ=0 NormalX=0 NormalY=0 NormalZ=1 AngleXU=0 Radius=1
    g6: Circle CenterX=-4.8 CenterY=1e-16 CenterZ=0 NormalX=0 NormalY=0 NormalZ=1 AngleXU=0 Radius=1
    g7: BSplineCurve PolesCount=3 KnotsCount=2 Degree=2 IsPeriodic=0
    g8: GeomPoint X=-3.5 Y=1.3 Z=0
    g9: GeomPoint X=-4.8 Y=1e-16 Z=0
    g10: LineSegment StartX=-3.5 StartY=1.3 StartZ=0 EndX=-3.5 EndY=1.5 EndZ=0
  constraints (24):
    c: Horizontal(g0)
    c: Distance(g0) = 1.9
    c: Block(g0)
    c: Coincident(g1,g0)
    c: Vertical(g1)
    c: Coincident(g2,g1)
    c: Horizontal(g2)
    c: Coincident(g3,g0)
    c: Horizontal(g3)
    c: Distance(g3) = 1.3
    c: Weight(g4) = 1
    c: Equal(g4,g5)
    c: Coincident(g5,g0)
    c: Equal(g4,g6)
    c: Coincident(g7,g3)
    c: InternalAlignment(g4,g7)
    c: InternalAlignment(g5,g7)
    c: InternalAlignment(g6,g7)
    c: InternalAlignment(g8,g7)
    c: InternalAlignment(g9,g7)
    c: Coincident(g10,g7)
    c: Coincident(g10,g2)
    c: Vertical(g10)
    c: Block(g10)
FEATURE [Part::Feature] Face035
  shape: bbox 3.2 x 1.5 x 2e-07 mm, 1 faces, 0 solids (baked)
FEATURE [Part::Revolution] Revolve039  label="backCaseScrewRetainer"
  Angle = 360
  Axis = (0,1,0)
  Base = (0,0,0)
  FaceMakerClass = Part::FaceMakerBullseye
  Placement = pos=(12.5,3,62) rot=(0,0,1;0rad)
  Solid = false
  Source = -> Face035
  Symmetric = false
FEATURE [Part::Feature] Face036
  shape: bbox 3.2 x 1.5 x 2e-07 mm, 1 faces, 0 solids (baked)
FEATURE [Part::Revolution] Revolve040  label="backCaseScrewRetainer001"
  Angle = 360
  Axis = (0,1,0)
  Base = (0,0,0)
  FaceMakerClass = Part::FaceMakerBullseye
  Placement = pos=(12.5,3,10) rot=(0,0,1;0rad)
  Solid = false
  Source = -> Face036
  Symmetric = false
FEATURE [Part::Feature] Face037
  shape: bbox 4.8 x 30.5 x 2e-07 mm, 1 faces, 0 solids (baked)
FEATURE [Part::Feature] Face038
  shape: bbox 4.8 x 30.5 x 2e-07 mm, 1 faces, 0 solids (baked)
FEATURE [Part::Feature] Face039
  shape: bbox 4.8 x 30.2 x 2e-07 mm, 1 faces, 0 solids (baked)
FEATURE [Part::Revolution] Revolve043  label="frontCaseScrewPost002"
  Angle = 360
  Axis = (0,1,0)
  Base = (0,0,0)
  FaceMakerClass = Part::FaceMakerBullseye
  Placement = pos=(89.5,4.5,3.5) rot=(0,0,1;0rad)
  Solid = false
  Source = -> Face039
  Symmetric = false
FEATURE [Part::Feature] Face040
  shape: bbox 4.8 x 30.2 x 2e-07 mm, 1 faces, 0 solids (baked)
FEATURE [Part::Revolution] Revolve044  label="moreFrontCaseScrewPost"
  Angle = 360
  Axis = (0,1,0)
  Base = (0,0,0)
  FaceMakerClass = Part::FaceMakerBullseye
  Placement = pos=(102.5,4.5,68.5) rot=(0,0,1;0rad)
  Solid = false
  Source = -> Face040
  Symmetric = false
FEATURE [Part::Feature] Face041
  shape: bbox 4.8 x 30.2 x 2e-07 mm, 1 faces, 0 solids (baked)
FEATURE [Part::Revolution] Revolve045  label="moreFrontCaseScrewPost004"
  Angle = 360
  Axis = (0,1,0)
  Base = (0,0,0)
  FaceMakerClass = Part::FaceMakerBullseye
  Placement = pos=(102.5,4.5,3.5) rot=(0,0,1;0rad)
  Solid = false
  Source = -> Face041
  Symmetric = false
FEATURE [Part::Feature] Face042
  shape: bbox 4.8 x 30.2 x 2e-07 mm, 1 faces, 0 solids (baked)
FEATURE [Part::Revolution] Revolve046  label="frontCaseScrewPost003"
  Angle = 360
  Axis = (0,1,0)
  Base = (0,0,0)
  FaceMakerClass = Part::FaceMakerBullseye
  Placement = pos=(89.5,4.5,68.5) rot=(0,0,1;0rad)
  Solid = false
  Source = -> Face042
  Symmetric = false
FEATURE [Part::Feature] Face043
  shape: bbox 3.2 x 1.5 x 2e-07 mm, 1 faces, 0 solids (baked)
FEATURE [Part::Revolution] Revolve047  label="frontCaseScrewRetainer002"
  Angle = 360
  Axis = (0,1,0)
  Base = (0,0,0)
  FaceMakerClass = Part::FaceMakerBullseye
  Placement = pos=(89.5,3,68.5) rot=(0,0,1;0rad)
  Solid = false
  Source = -> Face043
  Symmetric = false
FEATURE [Part::Feature] Face044
  shape: bbox 3.2 x 1.5 x 2e-07 mm, 1 faces, 0 solids (baked)
FEATURE [Part::Revolution] Revolve048  label="frontCaseScrewRetainer003"
  Angle = 360
  Axis = (0,1,0)
  Base = (0,0,0)
  FaceMakerClass = Part::FaceMakerBullseye
  Placement = pos=(89.5,3,3.5) rot=(0,0,1;0rad)
  Solid = false
  Source = -> Face044
  Symmetric = false
FEATURE [Part::Feature] Face045
  shape: bbox 4.8 x 30.2 x 2e-07 mm, 1 faces, 0 solids (baked)
FEATURE [Part::Revolution] Revolve049  label="backCaseScrewPost002"
  Angle = 360
  Axis = (0,1,0)
  Base = (0,0,0)
  FaceMakerClass = Part::FaceMakerBullseye
  Placement = pos=(12.5,4.5,62) rot=(0,0,1;0rad)
  Solid = false
  Source = -> Face045
  Symmetric = false
